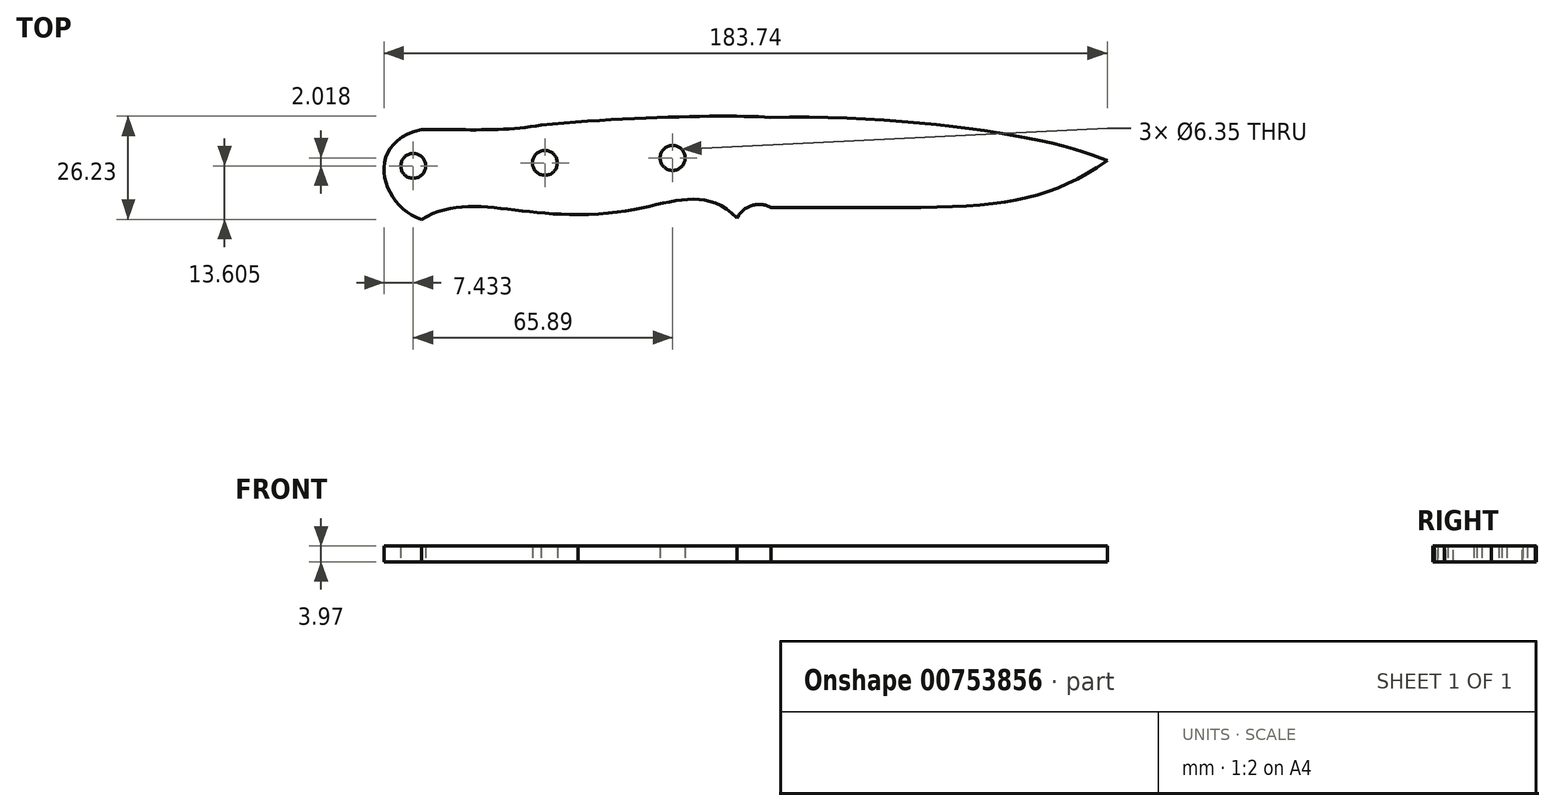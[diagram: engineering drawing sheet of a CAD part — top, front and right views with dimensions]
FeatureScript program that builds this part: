
annotation { "Feature Type Name" : "Feature", "Feature Type Description" : "" }
export const myFeature = defineFeature(function(context is Context, id is Id, definition is map)
    precondition{}
    {
        {
            var Q0;
            Q0=qCreatedBy(makeId("Top.planeOp"),FACE);
            var sketch = newSketch(context, id + "F0", { "sketchPlane" : qUnion([Q0])});
            skFitSpline(sketch, "E0", {"points": [v(93.1, 11.86) * mm, v(7.67, 0) * mm], "startDerivative": vector(-60.23, -41.07) * mm, "endDerivative": vector(-156.47, 0) * mm});
            skArc(sketch, "E1", {"start": v(7.67, 0) * mm, "mid": v(2.82, 0.5) * mm, "end": v(-0.9, -2.67) * mm});
            skFitSpline(sketch, "E2", {"points": [v(-0.9, -2.67) * mm, v(-41.3, -1.82) * mm], "startDerivative": vector(-32.4, 31.1) * mm, "endDerivative": vector(-62.7, 0.67) * mm});
            skFitSpline(sketch, "E3", {"points": [v(-41.3, -1.82) * mm, v(-81.15, -3.04) * mm], "startDerivative": vector(-51, -0.25) * mm, "endDerivative": vector(-32.43, -19.82) * mm});
            skFitSpline(sketch, "E4", {"points": [v(-81.15, -3.04) * mm, v(-81.15, 19.83) * mm], "startDerivative": vector(-30.1, 9.11) * mm, "endDerivative": vector(45.08, 10.16) * mm});
            skFitSpline(sketch, "E5", {"points": [v(-81.15, 19.83) * mm, v(-50.73, 20.96) * mm], "startDerivative": vector(25.5, 0.36) * mm, "endDerivative": vector(30.3, 5.7) * mm});
            skFitSpline(sketch, "E6", {"points": [v(-50.73, 20.96) * mm, v(7.36, 22.86) * mm], "startDerivative": vector(66.3, 6.24) * mm, "endDerivative": vector(29.4, -2.32) * mm});
            skFitSpline(sketch, "E7", {"points": [v(7.36, 22.86) * mm, v(93.1, 11.86) * mm], "startDerivative": vector(115.48, 2.32) * mm, "endDerivative": vector(37.82, -17.31) * mm});
            skCircle(sketch, "E8", {"center": v(-49.78, 11.33) * mm, "radius": 3.17 * mm, "construction": true});
            skCircle(sketch, "E9", {"center": v(-17.32, 12.58) * mm, "radius": 3.17 * mm, "construction": true});
            skCircle(sketch, "E10", {"center": v(-83.2, 10.56) * mm, "radius": 3.17 * mm, "construction": true});
            skSolve(sketch);
        }
        {
            var Q0;
            Q0=makeQuery(id+"F0.imprint","IMPRINT",FACE,{"disambiguationData":[TD([[makeQuery(id+"F0.imprint","IMPRINT",EDGE,{"derivedFrom":sQuery(id+"F0.wireOp",EDGE,"E0")}),-1.0]])]});
            extrude(context, id + "F1", {"entities" : qUnion([Q0]), "depth" : 3.97 * mm, "offsetDistance" : 25.4 * mm});
        }
        {
            var Q0;
            Q0=sQuery(id+"F0.wireOp",VERTEX,"E8.center");
            var Q1;
            Q1=makeQuery(id+"F1.opExtrude","SWEPT_BODY",BODY,{"disambiguationData":[OSD([sQuery(id+"F0.wireOp",EDGE,"E0"),sQuery(id+"F0.wireOp",EDGE,"E1"),sQuery(id+"F0.wireOp",EDGE,"E2"),sQuery(id+"F0.wireOp",EDGE,"E3"),sQuery(id+"F0.wireOp",EDGE,"E4"),sQuery(id+"F0.wireOp",EDGE,"E5"),sQuery(id+"F0.wireOp",EDGE,"E6"),sQuery(id+"F0.wireOp",EDGE,"E7")])]});
            hole(context, id + "F2", {"style" : HoleStyle.SIMPLE, "endStyle" : HoleEndStyle.THROUGH, "oppositeDirection" : true, "holeDiameter" : 6.35 * mm, "majorDiameter" : 6.35 * mm, "isTappedThrough" : true, "tappedDepth" : 12.7 * mm, "tapClearance" : 3, "locations" : qUnion([Q0]), "scope" : qUnion([Q1])});
        }
        {
            var Q0;
            Q0=sQuery(id+"F0.wireOp",VERTEX,"E10.center");
            var Q1;
            Q1=sQuery(id+"F0.wireOp",VERTEX,"E9.center");
            var Q2;
            Q2=makeQuery(id+"F1.opExtrude","SWEPT_BODY",BODY,{"disambiguationData":[OSD([sQuery(id+"F0.wireOp",EDGE,"E0"),sQuery(id+"F0.wireOp",EDGE,"E1"),sQuery(id+"F0.wireOp",EDGE,"E2"),sQuery(id+"F0.wireOp",EDGE,"E3"),sQuery(id+"F0.wireOp",EDGE,"E4"),sQuery(id+"F0.wireOp",EDGE,"E5"),sQuery(id+"F0.wireOp",EDGE,"E6"),sQuery(id+"F0.wireOp",EDGE,"E7")])]});
            hole(context, id + "F3", {"style" : HoleStyle.SIMPLE, "endStyle" : HoleEndStyle.THROUGH, "oppositeDirection" : true, "holeDiameter" : 6.35 * mm, "majorDiameter" : 6.35 * mm, "isTappedThrough" : true, "tappedDepth" : 12.7 * mm, "tapClearance" : 3, "locations" : qUnion([Q0, Q1]), "scope" : qUnion([Q2])});
        }
    });
